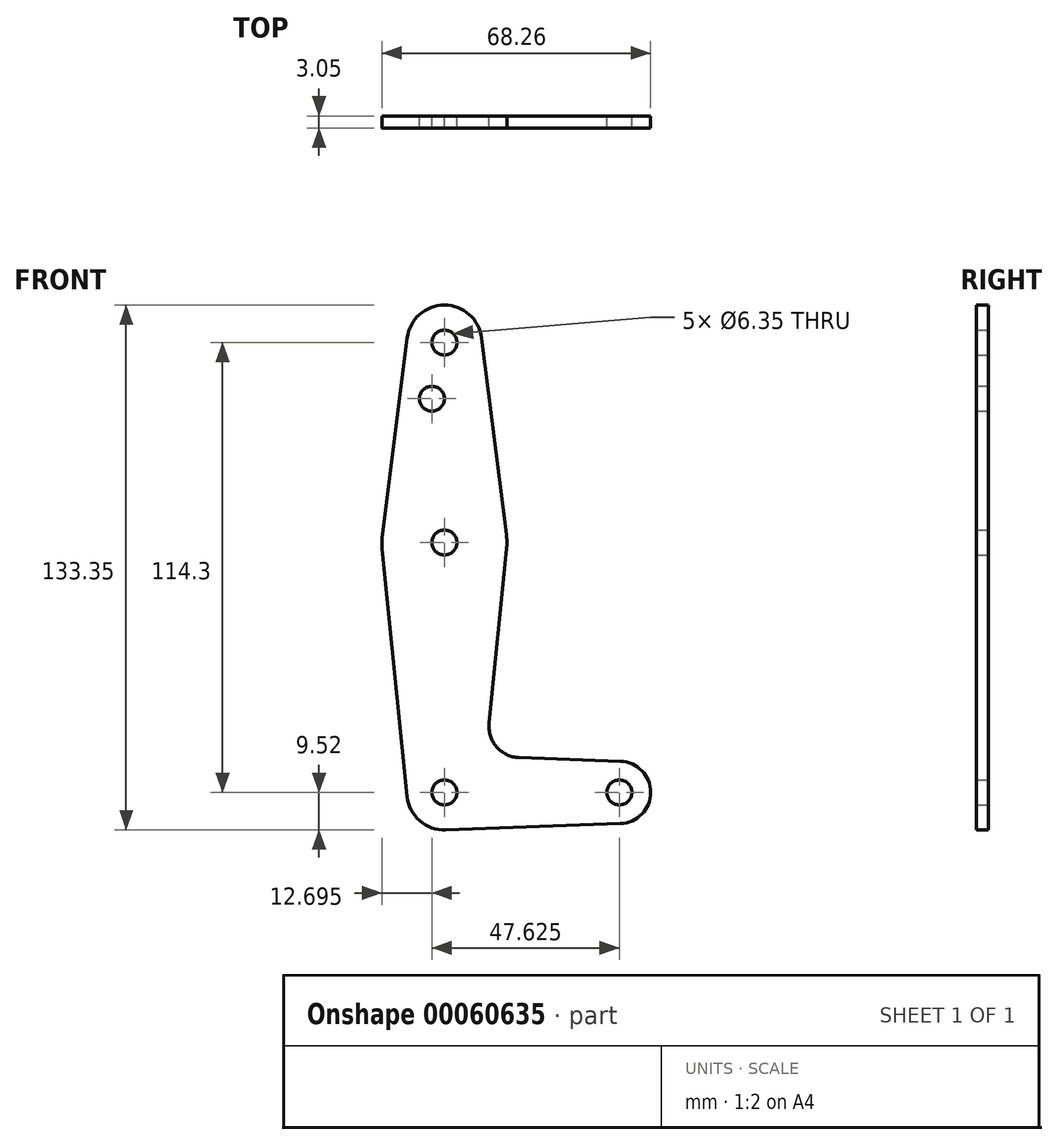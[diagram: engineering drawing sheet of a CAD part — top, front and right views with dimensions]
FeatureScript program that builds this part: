
annotation { "Feature Type Name" : "Feature", "Feature Type Description" : "" }
export const myFeature = defineFeature(function(context is Context, id is Id, definition is map)
    precondition{}
    {
        {
            var Q0;
            Q0=qCreatedBy(makeId("Front.planeOp"),FACE);
            var sketch = newSketch(context, id + "F0", { "sketchPlane" : qUnion([Q0])});
            skCircle(sketch, "E0", {"center": v(0, 0) * mm, "radius": 9.53 * mm});
            skLineSegment(sketch, "E1", {"start": v(0, 0) * mm, "end": v(0, 114.3) * mm, "construction": true});
            skLineSegment(sketch, "E2", {"start": v(0, 0) * mm, "end": v(44.45, 0) * mm, "construction": true});
            skCircle(sketch, "E3", {"center": v(44.45, 0) * mm, "radius": 7.94 * mm});
            skCircle(sketch, "E4", {"center": v(0, 114.3) * mm, "radius": 9.53 * mm});
            skCircle(sketch, "E5", {"center": v(0, 63.5) * mm, "radius": 15.88 * mm});
            skLineSegment(sketch, "E6", {"start": v(-9.45, 115.5) * mm, "end": v(-15.75, 65.48) * mm});
            skLineSegment(sketch, "E7", {"start": v(-9.48, -0.95) * mm, "end": v(-15.8, 61.91) * mm});
            skLineSegment(sketch, "E8", {"start": v(11.34, 17.6) * mm, "end": v(15.8, 61.91) * mm});
            skLineSegment(sketch, "E9", {"start": v(9.45, 115.5) * mm, "end": v(15.8, 65.13) * mm});
            skLineSegment(sketch, "E10", {"start": v(44.73, 7.93) * mm, "end": v(18.97, 8.85) * mm});
            skCircle(sketch, "E11", {"center": v(0, 114.3) * mm, "radius": 3.18 * mm});
            skCircle(sketch, "E12", {"center": v(-3.18, 100.03) * mm, "radius": 3.18 * mm});
            skCircle(sketch, "E13", {"center": v(0, 63.5) * mm, "radius": 3.18 * mm});
            skCircle(sketch, "E14", {"center": v(0, 0) * mm, "radius": 3.18 * mm});
            skCircle(sketch, "E15", {"center": v(44.45, 0) * mm, "radius": 3.18 * mm});
            skArc(sketch, "E16.filletArc", {"start": v(11.34, 17.6) * mm, "mid": v(13.26, 11.57) * mm, "end": v(18.97, 8.85) * mm});
            skLineSegment(sketch, "E17", {"start": v(0.34, -9.52) * mm, "end": v(44.73, -7.93) * mm});
            skSolve(sketch);
        }
        {
            var Q0;
            Q0=makeQuery(id+"F0.imprint","IMPRINT",FACE,{"disambiguationData":[TD([[makeQuery(id+"F0.imprint","IMPRINT",EDGE,{"derivedFrom":sQuery(id+"F0.wireOp",EDGE,"E11")}),-1.0]])]});
            var Q1;
            {var subQ5=sQuery(id+"F0.wireOp",EDGE,"E6");Q1=makeQuery(id+"F0.imprint","IMPRINT",FACE,{"disambiguationData":[TD([[makeQuery(id+"F0.imprint","IMPRINT",EDGE,{"derivedFrom":subQ5}),1.0]])]});}
            var Q2;
            Q2=makeQuery(id+"F0.imprint","IMPRINT",FACE,{"disambiguationData":[TD([[makeQuery(id+"F0.imprint","IMPRINT",EDGE,{"derivedFrom":sQuery(id+"F0.wireOp",EDGE,"E13")}),-1.0]])]});
            var Q3;
            {var subQ0=sQuery(id+"F0.wireOp",EDGE,"E7");Q3=makeQuery(id+"F0.imprint","IMPRINT",FACE,{"disambiguationData":[TD([[makeQuery(id+"F0.imprint","IMPRINT",EDGE,{"derivedFrom":subQ0}),-1.0]])]});}
            var Q4;
            Q4=makeQuery(id+"F0.imprint","IMPRINT",FACE,{"disambiguationData":[TD([[makeQuery(id+"F0.imprint","IMPRINT",EDGE,{"derivedFrom":sQuery(id+"F0.wireOp",EDGE,"E14")}),-1.0]])]});
            var Q5;
            Q5=makeQuery(id+"F0.imprint","IMPRINT",FACE,{"disambiguationData":[TD([[makeQuery(id+"F0.imprint","IMPRINT",EDGE,{"derivedFrom":sQuery(id+"F0.wireOp",EDGE,"E15")}),-1.0]])]});
            extrude(context, id + "F1", {"entities" : qUnion([Q0, Q1, Q2, Q3, Q4, Q5]), "depth" : 3.05 * mm});
        }
    });
